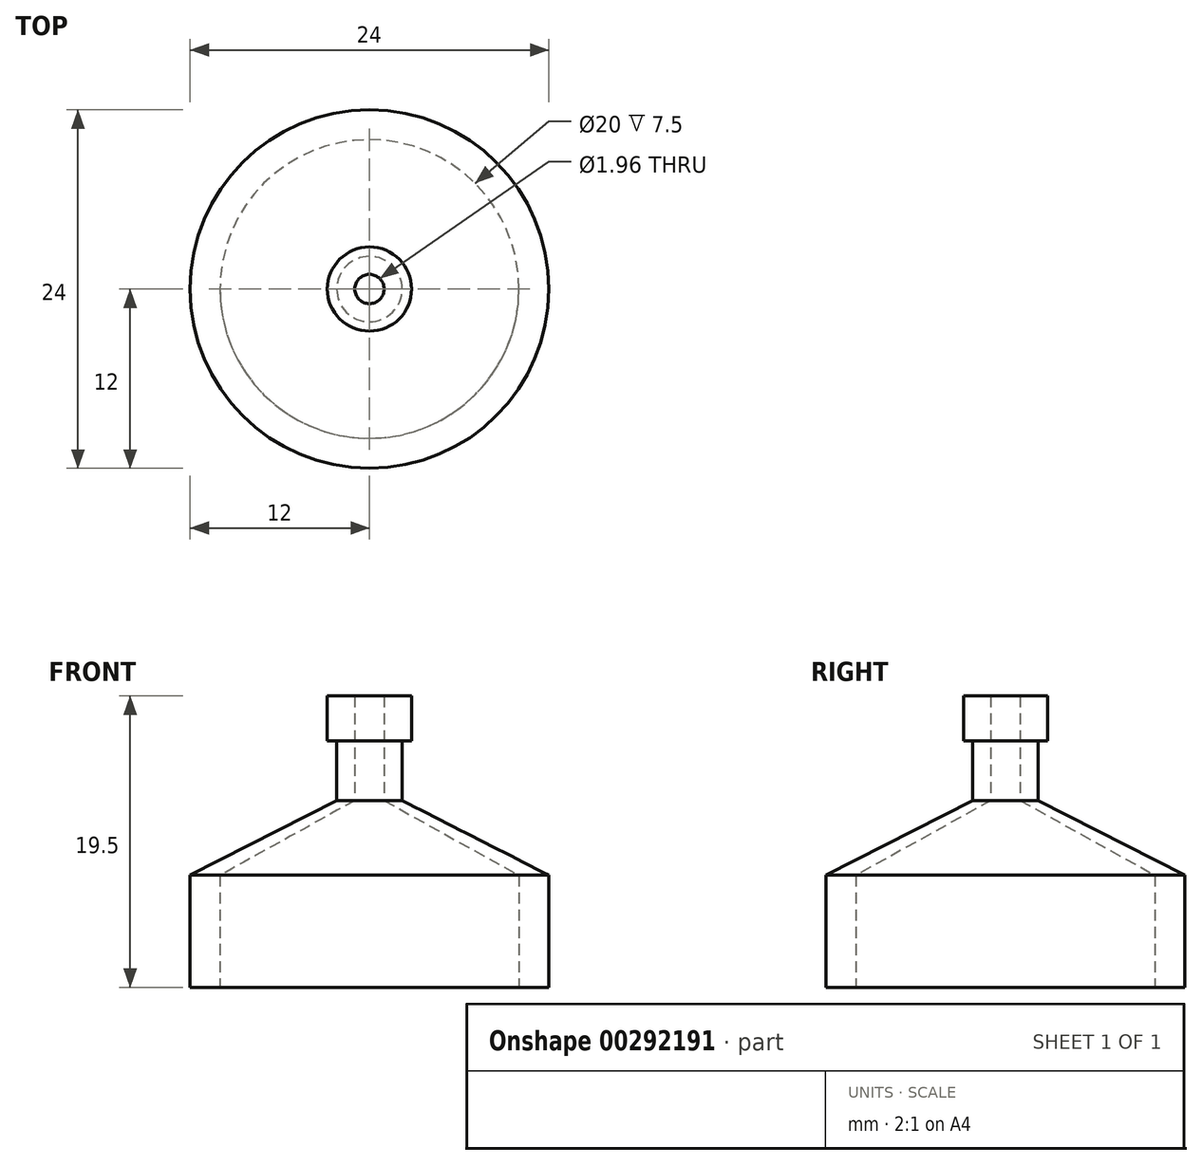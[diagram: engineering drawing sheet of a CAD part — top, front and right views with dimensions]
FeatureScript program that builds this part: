
annotation { "Feature Type Name" : "Feature", "Feature Type Description" : "" }
export const myFeature = defineFeature(function(context is Context, id is Id, definition is map)
    precondition{}
    {
        {
            var Q0;
            Q0=qCreatedBy(makeId("Top.planeOp"),FACE);
            var sketch = newSketch(context, id + "F0", { "sketchPlane" : qUnion([Q0])});
            skCircle(sketch, "E0", {"center": v(0, 0) * mm, "radius": 10 * mm});
            skCircle(sketch, "E1", {"center": v(0, 0) * mm, "radius": 12 * mm});
            skSolve(sketch);
        }
        {
            var Q0;
            Q0=makeQuery(id+"F0.imprint","IMPRINT",FACE,{"disambiguationData":[TD([[makeQuery(id+"F0.imprint","IMPRINT",EDGE,{"derivedFrom":sQuery(id+"F0.wireOp",EDGE,"E0")}),-1.0]])]});
            extrude(context, id + "F1", {"entities" : qUnion([Q0]), "depth" : 7.5 * mm});
        }
        {
            var Q0;
            Q0=makeQuery(id+"F1.opExtrude","CAP_FACE",FACE,{"disambiguationData":[OSD([sQuery(id+"F0.wireOp",EDGE,"E0"),sQuery(id+"F0.wireOp",EDGE,"E1")])],"isStart":false});
            var sketch = newSketch(context, id + "F2", { "sketchPlane" : qUnion([Q0])});
            skCircle(sketch, "E2", {"center": v(0, 0) * mm, "radius": 12 * mm});
            skSolve(sketch);
        }
        {
            var Q0;
            Q0 = qSketchRegion(id + "F2", true);
            extrude(context, id + "F3", {"entities" : qUnion([Q0]), "operationType" : NewBodyOperationType.ADD, "depth" : 5 * mm, "hasDraft" : true, "draftAngle" : 63 * degree, "draftPullDirection" : true});
        }
        {
            var Q0;
            Q0=makeQuery(id+"F3.opExtrude","CAP_FACE",FACE,{"disambiguationData":[OSD([sQuery(id+"F2.wireOp",EDGE,"E2")])],"isStart":true});
            var sketch = newSketch(context, id + "F4", { "sketchPlane" : qUnion([Q0])});
            skCircle(sketch, "E3", {"center": v(0, 0) * mm, "radius": 10 * mm});
            skSolve(sketch);
        }
        {
            var Q0;
            Q0 = qSketchRegion(id + "F4", true);
            extrude(context, id + "F5", {"entities" : qUnion([Q0]), "operationType" : NewBodyOperationType.REMOVE, "oppositeDirection" : true, "depth" : 5 * mm, "hasDraft" : true, "draftAngle" : 61 * degree, "draftPullDirection" : true});
        }
        {
            var Q0;
            Q0=makeQuery(id+"F3.opExtrude","CAP_FACE",FACE,{"disambiguationData":[OSD([sQuery(id+"F2.wireOp",EDGE,"E2")])],"isStart":false});
            var sketch = newSketch(context, id + "F6", { "sketchPlane" : qUnion([Q0])});
            skSolve(sketch);
        }
        {
            var Q0;
            Q0=makeQuery(id+"F6.imprint","IMPRINT",FACE,{"disambiguationData":[TD([[makeQuery(id+"F6.imprint","IMPRINT",EDGE,{"derivedFrom":makeQuery(id+"F3.opExtrude","CAP_EDGE",EDGE,{"disambiguationData":[OSD([sQuery(id+"F2.wireOp",EDGE,"E2")])],"isStart":false})}),1.0]])]});
            extrude(context, id + "F7", {"entities" : qUnion([Q0]), "operationType" : NewBodyOperationType.ADD, "depth" : 4 * mm});
        }
        {
            var Q0;
            Q0=makeQuery(id+"F7.opExtrude","CAP_FACE",FACE,{"disambiguationData":[OSD([sQuery(id+"F2.wireOp",EDGE,"E2"),sQuery(id+"F4.wireOp",EDGE,"E3")])],"isStart":false});
            var sketch = newSketch(context, id + "F8", { "sketchPlane" : qUnion([Q0])});
            skCircle(sketch, "E4", {"center": v(0, 0) * mm, "radius": 2.82 * mm});
            skSolve(sketch);
        }
        {
            var Q0;
            Q0=makeQuery(id+"F8.imprint","IMPRINT",FACE,{"disambiguationData":[TD([[makeQuery(id+"F8.imprint","IMPRINT",EDGE,{"derivedFrom":makeQuery(id+"F7.opExtrude","CAP_EDGE",EDGE,{"disambiguationData":[OSD([sQuery(id+"F2.wireOp",EDGE,"E2")])],"isStart":false})}),1.0]])]});
            var Q1;
            Q1=makeQuery(id+"F8.imprint","IMPRINT",FACE,{"disambiguationData":[TD([[makeQuery(id+"F8.imprint","IMPRINT",EDGE,{"derivedFrom":sQuery(id+"F8.wireOp",EDGE,"E4")}),1.0]])]});
            extrude(context, id + "F9", {"entities" : qUnion([Q0, Q1]), "operationType" : NewBodyOperationType.ADD, "depth" : 3 * mm});
        }
    });
